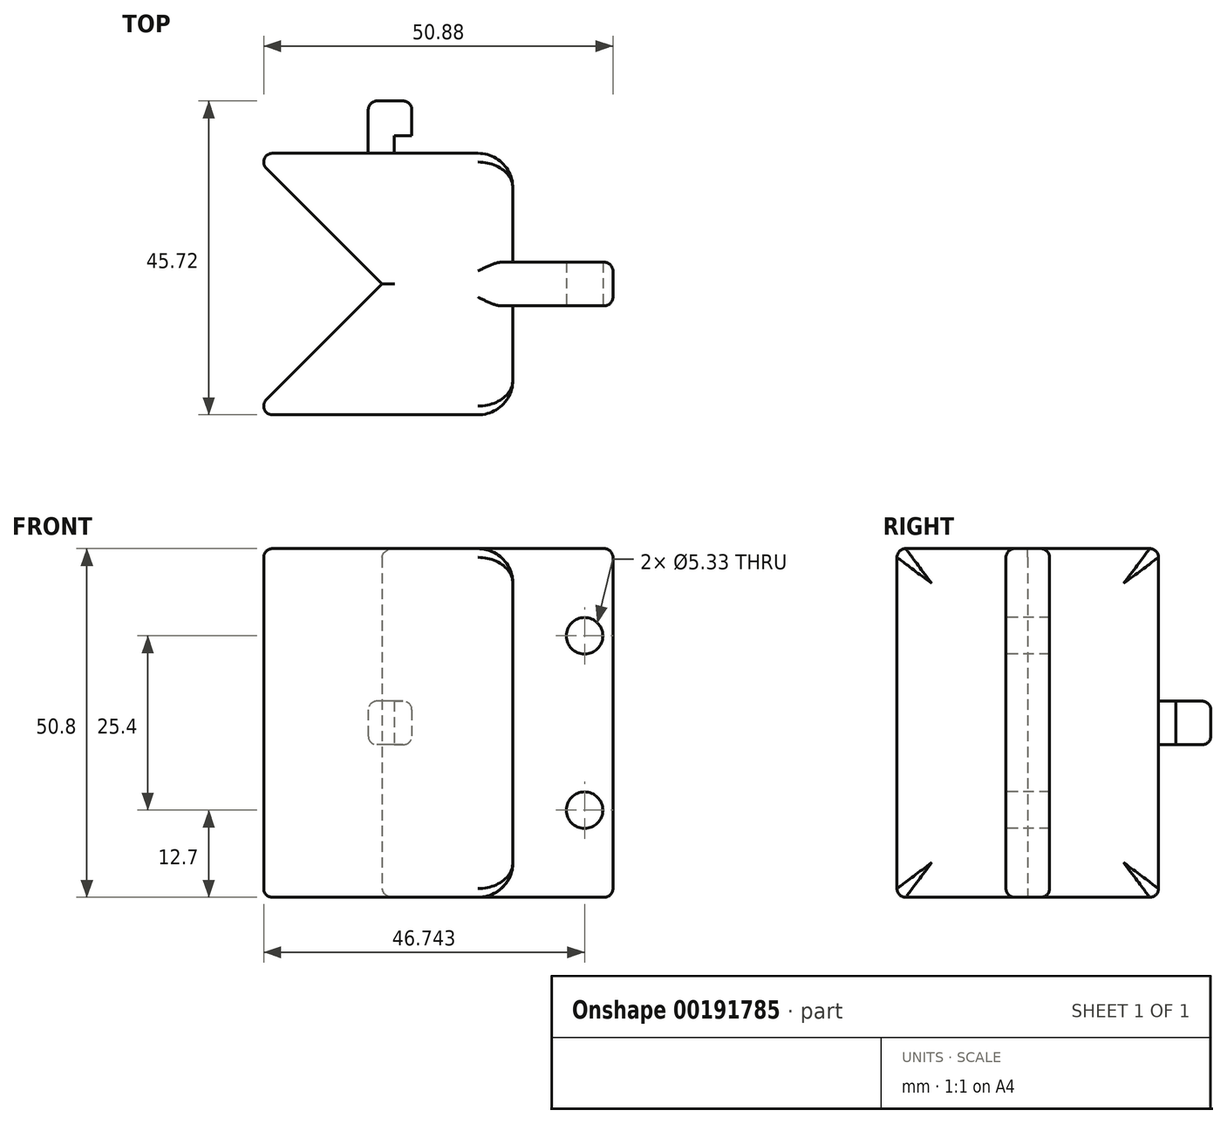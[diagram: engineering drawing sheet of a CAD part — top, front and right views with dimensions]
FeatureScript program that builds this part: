
annotation { "Feature Type Name" : "Feature", "Feature Type Description" : "" }
export const myFeature = defineFeature(function(context is Context, id is Id, definition is map)
    precondition{}
    {
        {
            var Q0;
            Q0=qCreatedBy(makeId("Top.planeOp"),FACE);
            var sketch = newSketch(context, id + "F0", { "sketchPlane" : qUnion([Q0])});
            skLineSegment(sketch, "E0.bottom", {"start": v(-59.3, -5.95) * mm, "end": v(-21.2, -5.95) * mm});
            skLineSegment(sketch, "E0.top", {"start": v(-59.3, -44.05) * mm, "end": v(-21.2, -44.05) * mm});
            skLineSegment(sketch, "E0.right", {"start": v(-21.2, -5.95) * mm, "end": v(-21.2, -44.05) * mm});
            skLineSegment(sketch, "E1", {"start": v(-59.3, -5.95) * mm, "end": v(-40.25, -25) * mm});
            skLineSegment(sketch, "E2", {"start": v(-40.25, -25) * mm, "end": v(-59.3, -44.05) * mm});
            skLineSegment(sketch, "E3.bottom", {"start": v(-21.2, -21.83) * mm, "end": v(-6.63, -21.83) * mm});
            skLineSegment(sketch, "E3.top", {"start": v(-21.2, -28.18) * mm, "end": v(-6.63, -28.18) * mm});
            skLineSegment(sketch, "E3.left", {"start": v(-21.2, -21.83) * mm, "end": v(-21.2, -28.18) * mm});
            skLineSegment(sketch, "E3.right", {"start": v(-6.63, -21.83) * mm, "end": v(-6.63, -28.18) * mm});
            skSolve(sketch);
        }
        {
            var Q0;
            Q0=makeQuery(id+"F0.imprint","IMPRINT",FACE,{"disambiguationData":[TD([[makeQuery(id+"F0.imprint","IMPRINT",EDGE,{"derivedFrom":sQuery(id+"F0.wireOp",EDGE,"E0.bottom")}),-1.0]])]});
            var Q1;
            Q1=makeQuery(id+"F0.imprint","IMPRINT",FACE,{"disambiguationData":[TD([[makeQuery(id+"F0.imprint","IMPRINT",EDGE,{"derivedFrom":sQuery(id+"F0.wireOp",EDGE,"E3.bottom")}),-1.0]])]});
            extrude(context, id + "F1", {"entities" : qUnion([Q0, Q1]), "depth" : 50.8 * mm});
        }
        {
            var Q0;
            Q0=makeQuery(id+"F1.opExtrude","CAP_EDGE",EDGE,{"disambiguationData":[OSD([sQuery(id+"F0.wireOp",EDGE,"E0.bottom")])],"isStart":true});
            var Q1;
            Q1=makeQuery(id+"F1.opExtrude","CAP_EDGE",EDGE,{"disambiguationData":[OSD([sQuery(id+"F0.wireOp",EDGE,"E0.bottom")])],"isStart":false});
            var Q2;
            Q2=makeQuery(id+"F1.opExtrude","SWEPT_EDGE",EDGE,{"disambiguationData":[OSD([sQuery(id+"F0.wireOp",EDGE,"E0.bottom"),sQuery(id+"F0.wireOp",EDGE,"E1")])]});
            var Q3;
            Q3=makeQuery(id+"F1.opExtrude","CAP_EDGE",EDGE,{"disambiguationData":[OSD([sQuery(id+"F0.wireOp",EDGE,"E0.top")])],"isStart":false});
            var Q4;
            Q4=makeQuery(id+"F1.opExtrude","SWEPT_EDGE",EDGE,{"disambiguationData":[OSD([sQuery(id+"F0.wireOp",EDGE,"E0.top"),sQuery(id+"F0.wireOp",EDGE,"E2")])]});
            var Q5;
            Q5=makeQuery(id+"F1.opExtrude","CAP_EDGE",EDGE,{"disambiguationData":[OSD([sQuery(id+"F0.wireOp",EDGE,"E0.top")])],"isStart":true});
            var Q6;
            Q6=makeQuery(id+"F1.opExtrude","CAP_EDGE",EDGE,{"disambiguationData":[OSD([sQuery(id+"F0.wireOp",EDGE,"E2")])],"isStart":true});
            var Q7;
            Q7=makeQuery(id+"F1.opExtrude","CAP_EDGE",EDGE,{"disambiguationData":[OSD([sQuery(id+"F0.wireOp",EDGE,"E1")])],"isStart":true});
            var Q8;
            Q8=makeQuery(id+"F1.opExtrude","CAP_EDGE",EDGE,{"disambiguationData":[OSD([sQuery(id+"F0.wireOp",EDGE,"E2")])],"isStart":false});
            var Q9;
            Q9=makeQuery(id+"F1.opExtrude","CAP_EDGE",EDGE,{"disambiguationData":[OSD([sQuery(id+"F0.wireOp",EDGE,"E1")])],"isStart":false});
            fillet(context, id + "F2", {"entities" : qUnion([Q0, Q1, Q2, Q3, Q4, Q5, Q6, Q7, Q8, Q9]), "radius" : 1.27 * mm, "tangentPropagation" : true, "allowEdgeOverflow" : false});
        }
        {
            var Q0;
            Q0=makeQuery(id+"F1.opExtrude","SWEPT_FACE",FACE,{"disambiguationData":[OSD([sQuery(id+"F0.wireOp",EDGE,"E3.top")])]});
            var sketch = newSketch(context, id + "F3", { "sketchPlane" : qUnion([Q0])});
            skCircle(sketch, "E4", {"center": v(-10.77, 38.1) * mm, "radius": 2.67 * mm});
            skCircle(sketch, "E5", {"center": v(-10.77, 12.7) * mm, "radius": 2.67 * mm});
            skSolve(sketch);
        }
        {
            var Q0;
            Q0 = qSketchRegion(id + "F3", true);
            extrude(context, id + "F4", {"entities" : qUnion([Q0]), "operationType" : NewBodyOperationType.REMOVE, "oppositeDirection" : true, "depth" : 25.4 * mm});
        }
        {
            var Q0;
            Q0=makeQuery(id+"F1.opExtrude","SWEPT_EDGE",EDGE,{"disambiguationData":[OSD([sQuery(id+"F0.wireOp",EDGE,"E0.bottom"),sQuery(id+"F0.wireOp",EDGE,"E0.right")])]});
            var Q1;
            Q1=makeQuery(id+"F1.opExtrude","SWEPT_EDGE",EDGE,{"disambiguationData":[OSD([sQuery(id+"F0.wireOp",EDGE,"E0.top"),sQuery(id+"F0.wireOp",EDGE,"E0.right")])]});
            fillet(context, id + "F5", {"entities" : qUnion([Q0, Q1]), "radius" : 5.08 * mm, "tangentPropagation" : true, "allowEdgeOverflow" : false});
        }
        {
            var Q0;
            Q0=makeQuery(id+"F1.opExtrude","CAP_EDGE",EDGE,{"disambiguationData":[OSD([sQuery(id+"F0.wireOp",EDGE,"E3.top")])],"isStart":true});
            var Q1;
            Q1=makeQuery(id+"F1.opExtrude","SWEPT_EDGE",EDGE,{"disambiguationData":[OSD([sQuery(id+"F0.wireOp",EDGE,"E3.top"),sQuery(id+"F0.wireOp",EDGE,"E3.right")])]});
            var Q2;
            Q2=makeQuery(id+"F1.opExtrude","CAP_EDGE",EDGE,{"disambiguationData":[OSD([sQuery(id+"F0.wireOp",EDGE,"E3.top")])],"isStart":false});
            var Q3;
            Q3=makeQuery(id+"F1.opExtrude","CAP_EDGE",EDGE,{"disambiguationData":[OSD([sQuery(id+"F0.wireOp",EDGE,"E3.bottom")])],"isStart":true});
            var Q4;
            Q4=makeQuery(id+"F1.opExtrude","CAP_EDGE",EDGE,{"disambiguationData":[OSD([sQuery(id+"F0.wireOp",EDGE,"E3.bottom")])],"isStart":false});
            var Q5;
            Q5=makeQuery(id+"F1.opExtrude","SWEPT_EDGE",EDGE,{"disambiguationData":[OSD([sQuery(id+"F0.wireOp",EDGE,"E3.bottom"),sQuery(id+"F0.wireOp",EDGE,"E3.right")])]});
            var Q6;
            Q6=makeQuery(id+"F1.opExtrude","CAP_EDGE",EDGE,{"disambiguationData":[OSD([sQuery(id+"F0.wireOp",EDGE,"E3.right")])],"isStart":false});
            var Q7;
            Q7=makeQuery(id+"F1.opExtrude","CAP_EDGE",EDGE,{"disambiguationData":[OSD([sQuery(id+"F0.wireOp",EDGE,"E3.right")])],"isStart":true});
            fillet(context, id + "F6", {"entities" : qUnion([Q0, Q1, Q2, Q3, Q4, Q5, Q6, Q7]), "radius" : 1.27 * mm, "tangentPropagation" : true, "allowEdgeOverflow" : false});
        }
        {
            var Q0;
            Q0=makeQuery(id+"F1.opExtrude","SWEPT_FACE",FACE,{"disambiguationData":[OSD([sQuery(id+"F0.wireOp",EDGE,"E0.bottom")])]});
            var sketch = newSketch(context, id + "F7", { "sketchPlane" : qUnion([Q0])});
            skLineSegment(sketch, "E6.bottom", {"start": v(35.93, 28.58) * mm, "end": v(42.28, 28.58) * mm});
            skLineSegment(sketch, "E6.top", {"start": v(35.93, 22.23) * mm, "end": v(42.28, 22.23) * mm});
            skLineSegment(sketch, "E6.left", {"start": v(35.93, 28.58) * mm, "end": v(35.93, 22.23) * mm});
            skLineSegment(sketch, "E6.right", {"start": v(42.28, 28.58) * mm, "end": v(42.28, 22.23) * mm});
            skSolve(sketch);
        }
        {
            var Q0;
            Q0=makeQuery(id+"F7.imprint","IMPRINT",FACE,{"disambiguationData":[TD([[makeQuery(id+"F7.imprint","IMPRINT",EDGE,{"derivedFrom":sQuery(id+"F7.wireOp",EDGE,"E6.bottom")}),-1.0]])]});
            extrude(context, id + "F8", {"entities" : qUnion([Q0]), "operationType" : NewBodyOperationType.ADD, "depth" : 7.62 * mm});
        }
        {
            var Q0;
            Q0=makeQuery(id+"F8.opExtrude","SWEPT_FACE",FACE,{"disambiguationData":[OSD([sQuery(id+"F7.wireOp",EDGE,"E6.left")])]});
            var sketch = newSketch(context, id + "F9", { "sketchPlane" : qUnion([Q0])});
            skLineSegment(sketch, "E7.bottom", {"start": v(-5.95, 28.57) * mm, "end": v(-3.4, 28.57) * mm});
            skLineSegment(sketch, "E7.top", {"start": v(-5.95, 22.22) * mm, "end": v(-3.4, 22.22) * mm});
            skLineSegment(sketch, "E7.left", {"start": v(-5.95, 28.57) * mm, "end": v(-5.95, 22.22) * mm});
            skLineSegment(sketch, "E7.right", {"start": v(-3.4, 28.57) * mm, "end": v(-3.4, 22.22) * mm});
            skSolve(sketch);
        }
        {
            var Q0;
            Q0=makeQuery(id+"F9.imprint","IMPRINT",FACE,{"disambiguationData":[TD([[makeQuery(id+"F9.imprint","IMPRINT",EDGE,{"derivedFrom":sQuery(id+"F9.wireOp",EDGE,"E7.bottom")}),1.0]])]});
            extrude(context, id + "F10", {"entities" : qUnion([Q0]), "operationType" : NewBodyOperationType.REMOVE, "oppositeDirection" : true, "depth" : 2.54 * mm});
        }
        {
            var Q0;
            Q0=makeQuery(id+"F8.opExtrude","SWEPT_EDGE",EDGE,{"disambiguationData":[OSD([sQuery(id+"F7.wireOp",EDGE,"E6.bottom"),sQuery(id+"F7.wireOp",EDGE,"E6.left")])]});
            var Q1;
            Q1=makeQuery(id+"F8.opExtrude","CAP_EDGE",EDGE,{"disambiguationData":[OSD([sQuery(id+"F7.wireOp",EDGE,"E6.top")])],"isStart":false});
            var Q2;
            Q2=makeQuery(id+"F8.opExtrude","SWEPT_EDGE",EDGE,{"disambiguationData":[OSD([sQuery(id+"F7.wireOp",EDGE,"E6.top"),sQuery(id+"F7.wireOp",EDGE,"E6.left")])]});
            var Q3;
            Q3=makeQuery(id+"F8.opExtrude","CAP_EDGE",EDGE,{"disambiguationData":[OSD([sQuery(id+"F7.wireOp",EDGE,"E6.bottom")])],"isStart":false});
            var Q4;
            Q4=makeQuery(id+"F8.opExtrude","CAP_EDGE",EDGE,{"disambiguationData":[OSD([sQuery(id+"F7.wireOp",EDGE,"E6.left")])],"isStart":false});
            var Q5;
            Q5=makeQuery(id+"F10.boolean.opBoolean","COPY",EDGE,{"derivedFrom":makeQuery(id+"F10.opExtrude","CAP_EDGE",EDGE,{"disambiguationData":[OSD([sQuery(id+"F9.wireOp",EDGE,"E7.right")])],"isStart":true})});
            var Q6;
            Q6=makeQuery(id+"F8.opExtrude","SWEPT_EDGE",EDGE,{"disambiguationData":[OSD([sQuery(id+"F7.wireOp",EDGE,"E6.bottom"),sQuery(id+"F7.wireOp",EDGE,"E6.right")])]});
            var Q7;
            Q7=makeQuery(id+"F8.opExtrude","CAP_EDGE",EDGE,{"disambiguationData":[OSD([sQuery(id+"F7.wireOp",EDGE,"E6.right")])],"isStart":false});
            var Q8;
            Q8=makeQuery(id+"F8.opExtrude","SWEPT_EDGE",EDGE,{"disambiguationData":[OSD([sQuery(id+"F7.wireOp",EDGE,"E6.top"),sQuery(id+"F7.wireOp",EDGE,"E6.right")])]});
            var Q9;
            Q9=makeQuery(id+"F10.boolean.opBoolean","COPY",EDGE,{"derivedFrom":makeQuery(id+"F10.opExtrude","CAP_EDGE",EDGE,{"disambiguationData":[OSD([sQuery(id+"F9.wireOp",EDGE,"E7.bottom")])],"isStart":false})});
            var Q10;
            Q10=makeQuery(id+"F10.boolean.opBoolean","COPY",EDGE,{"derivedFrom":makeQuery(id+"F10.opExtrude","SWEPT_EDGE",EDGE,{"disambiguationData":[OSD([sQuery(id+"F7.wireOp",EDGE,"E6.bottom"),sQuery(id+"F7.wireOp",EDGE,"E6.left"),sQuery(id+"F9.wireOp",EDGE,"E7.bottom"),sQuery(id+"F9.wireOp",EDGE,"E7.right")])]})});
            var Q11;
            Q11=makeQuery(id+"F10.boolean.opBoolean","COPY",EDGE,{"derivedFrom":makeQuery(id+"F10.opExtrude","SWEPT_EDGE",EDGE,{"disambiguationData":[OSD([sQuery(id+"F7.wireOp",EDGE,"E6.top"),sQuery(id+"F7.wireOp",EDGE,"E6.left"),sQuery(id+"F9.wireOp",EDGE,"E7.top"),sQuery(id+"F9.wireOp",EDGE,"E7.right")])]})});
            var Q12;
            Q12=makeQuery(id+"F10.boolean.opBoolean","COPY",EDGE,{"derivedFrom":makeQuery(id+"F10.opExtrude","CAP_EDGE",EDGE,{"disambiguationData":[OSD([sQuery(id+"F9.wireOp",EDGE,"E7.top")])],"isStart":false})});
            fillet(context, id + "F11", {"entities" : qUnion([Q0, Q1, Q2, Q3, Q4, Q5, Q6, Q7, Q8, Q9, Q10, Q11, Q12]), "radius" : 1.27 * mm, "tangentPropagation" : true, "allowEdgeOverflow" : false});
        }
    });
